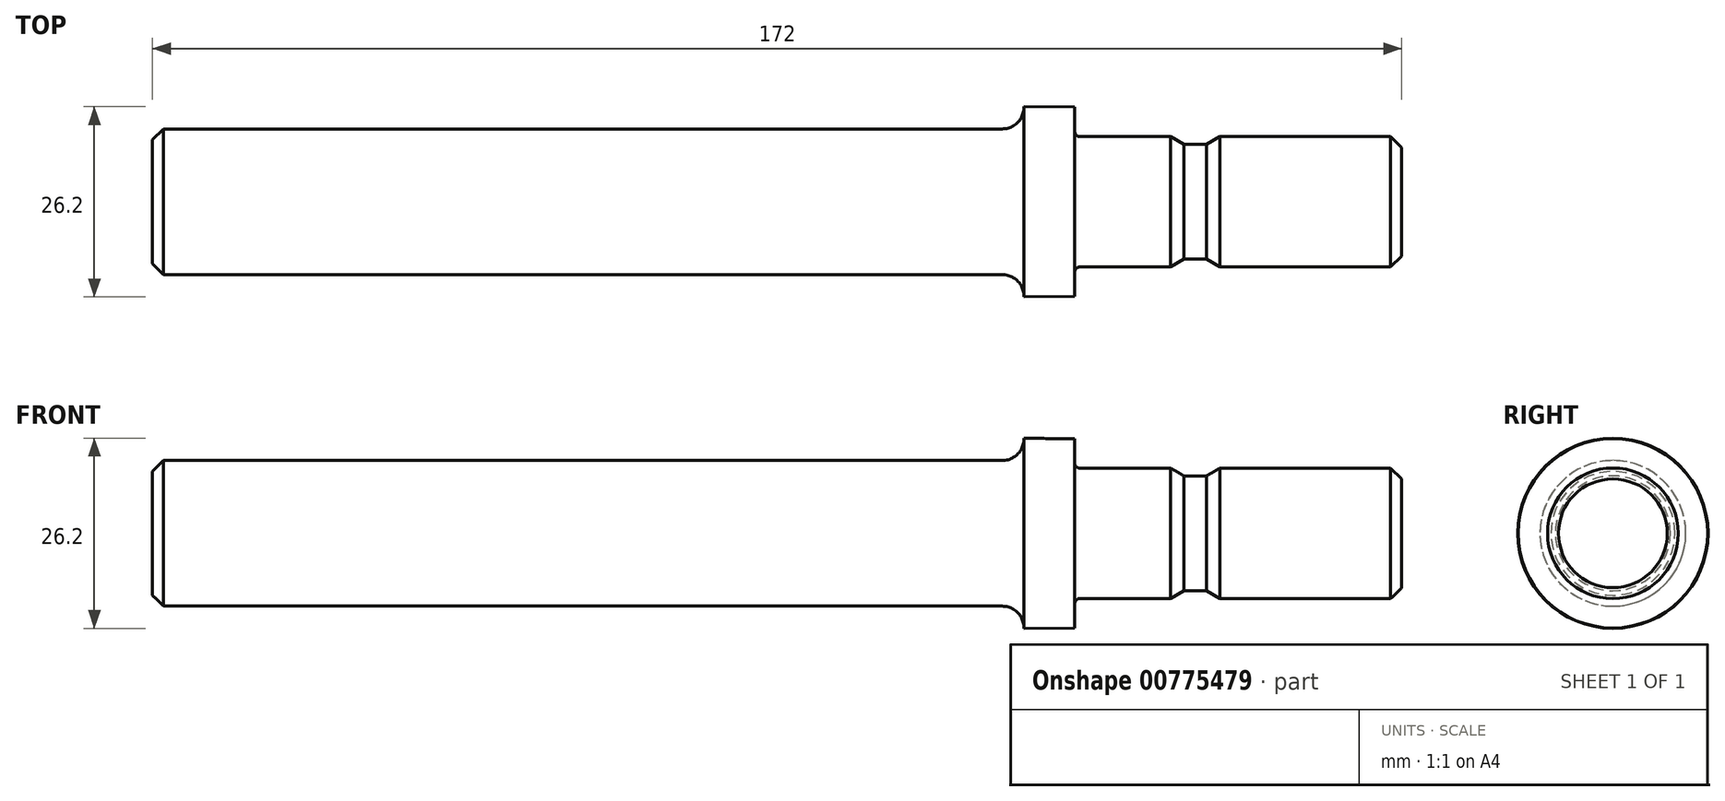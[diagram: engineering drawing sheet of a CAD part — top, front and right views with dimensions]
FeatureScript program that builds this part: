
annotation { "Feature Type Name" : "Feature", "Feature Type Description" : "" }
export const myFeature = defineFeature(function(context is Context, id is Id, definition is map)
    precondition{}
    {
        {
            var Q0;
            Q0=qCreatedBy(makeId("Front.planeOp"),FACE);
            var sketch = newSketch(context, id + "F0", { "sketchPlane" : qUnion([Q0])});
            skLineSegment(sketch, "E0", {"start": v(5, 13.04) * mm, "end": v(5, 13.1) * mm});
            skArc(sketch, "E1.filletArc", {"start": v(2, 10.04) * mm, "mid": v(4.12, 10.92) * mm, "end": v(5, 13.04) * mm});
            skLineSegment(sketch, "E2", {"start": v(5, 13.1) * mm, "end": v(12, 13.04) * mm});
            skLineSegment(sketch, "E3", {"start": v(2, 10.04) * mm, "end": v(-115, 10.04) * mm});
            skLineSegment(sketch, "E4", {"start": v(-115, 10.04) * mm, "end": v(-115, 0) * mm});
            skLineSegment(sketch, "E5", {"start": v(12, 13.04) * mm, "end": v(12, 9.62) * mm});
            skLineSegment(sketch, "E6", {"start": v(12.62, 9) * mm, "end": v(25.17, 9) * mm});
            skLineSegment(sketch, "E7", {"start": v(57, 9) * mm, "end": v(57, 0) * mm});
            skLineSegment(sketch, "E8", {"start": v(57, 9) * mm, "end": v(32, 9) * mm});
            skLineSegment(sketch, "E9", {"start": v(32, 9) * mm, "end": v(30.14, 7.91) * mm});
            skLineSegment(sketch, "E10", {"start": v(27.03, 7.91) * mm, "end": v(30.14, 7.91) * mm});
            skLineSegment(sketch, "E11.MirrorCS", {"start": v(25.17, 9) * mm, "end": v(27.03, 7.91) * mm});
            skArc(sketch, "E12.filletArc", {"start": v(12, 9.62) * mm, "mid": v(12.18, 9.18) * mm, "end": v(12.62, 9) * mm});
            skLineSegment(sketch, "E13.trimOffspring", {"start": v(32, 9) * mm, "end": v(57, 9) * mm});
            skLineSegment(sketch, "E14", {"start": v(-115, 0) * mm, "end": v(57, 0) * mm});
            skSolve(sketch);
        }
        {
            var Q0;
            Q0 = qSketchRegion(id + "F0", true);
            var Q1;
            Q1=sQuery(id+"F0.wireOp",EDGE,"E14");
            revolve(context, id + "F1", {"surfaceOperationType" : NewSurfaceOperationType.NEW, "entities" : qUnion([Q0]), "axis" : qUnion([Q1]), "revolveType" : RevolveType.FULL});
        }
        {
            var Q0;
            Q0=makeQuery(id+"F1.opRevolve","SWEPT_EDGE",EDGE,{"disambiguationData":[OSD([sQuery(id+"F0.wireOp",EDGE,"E7"),sQuery(id+"F0.wireOp",EDGE,"E13.trimOffspring")])]});
            chamfer(context, id + "F2", {"entities" : qUnion([Q0]), "width" : 1.5 * mm, "tangentPropagation" : true});
        }
        {
            var Q0;
            Q0=makeQuery(id+"F1.opRevolve","SWEPT_EDGE",EDGE,{"disambiguationData":[OSD([sQuery(id+"F0.wireOp",EDGE,"E3"),sQuery(id+"F0.wireOp",EDGE,"E4")])]});
            chamfer(context, id + "F3", {"entities" : qUnion([Q0]), "width" : 1.5 * mm, "tangentPropagation" : true});
        }
    });
